# Revit family: NL-SB42-Freestanding
name_source: partatom
category: Communication Devices
revit_build: Autodesk Revit 2018 (Build: 20190510_1515(x64)
units: mm (PartAtom-declared; Revit-internal decimal feet)

## family parameters
Cut with Voids When Loaded = No
Host = Face
Maintain Annotation Orientation = No
Part Type = Normal
Room Calculation Point = No
Round Connector Dimension = Use Diameter
Shared = No

## types (2) — shared parameters
Communication Ports = RJ45 Q-LAN
Coverage Horizontal = 150.00°
Coverage Vertical = 160.00°
Default Elevation = 0 mm
Depth = 83.3 mm
Height = 101 mm
Manufacturer = QSC, LLC
Manufacturer URL = http://www.qsc.com
Model = NL-SB42
Product Documentation Link = https://www.qsc.com
Product Page URL = https://www.qsc.com
Regulatory Compliance = UL/IEC 62368-1, CE
Temperature Max = 40° C
Temperature Min = 10° C
URL = https://www.qsc.com
Weight Dimensional (kg) = 3.57
Weight Dimensional (lb) = 7.86
Weight Product (kg) = 1.75
Weight Product (lb) = 3.86
Width = 518.1 mm

## per-type parameters (varying)
| type | Description | Power Handling | SPL Max |
| NL-SB42 PoE | Two-Way Network PoE Soundbar for Q-SYS | 12 | 106 |
| NL-SB42 Poe+ | Two-Way Network PoE+ Soundbar for Q-SYS | 24 | 107 |

## geometry (parser evidence)
native form markers: Sweep x2
no freeform markers — native parametric forms only
